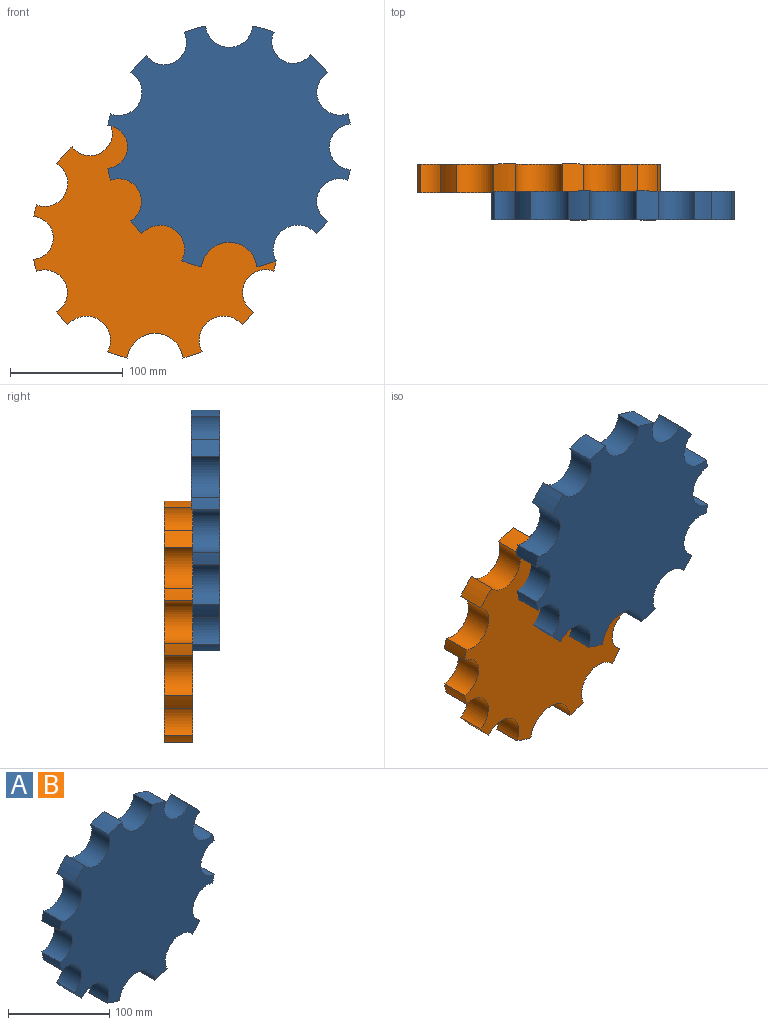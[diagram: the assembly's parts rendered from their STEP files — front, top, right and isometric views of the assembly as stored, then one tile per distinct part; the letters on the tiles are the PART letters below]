
ASSEMBLY  parts=2 mates=1
PART A: 26 faces, bbox 215.3x25.4x214 mm
  f0: cylinder r=19.08mm len=38.02mm, axis (0,1,0), area 1438.2mm2, adj f1,f23,f24,f25
  f1: cylinder r=109.44mm len=25.4mm, axis (0,1,0), area 278.4mm2, adj f0,f2,f24,f25
  f2: cylinder r=20.18mm len=37.37mm, axis (0,1,0), area 1515.7mm2, adj f1,f3,f24,f25
  f3: cylinder r=109.44mm len=25.4mm, axis (0,1,0), area 389mm2, adj f2,f4,f24,f25
  f4: cylinder r=21.37mm len=37.87mm, axis (0,1,0), area 1599.3mm2, adj f3,f5,f24,f25
  f5: cylinder r=109.44mm len=25.4mm, axis (0,1,0), area 469mm2, adj f4,f6,f24,f25
  f6: cylinder r=24.77mm len=49.23mm, axis (0,1,0), area 1834.1mm2, adj f5,f7,f24,f25
  f7: cylinder r=109.44mm len=25.4mm, axis (0,1,0), area 456mm2, adj f6,f8,f24,f25
  f8: cylinder r=21.61mm len=38.3mm, axis (0,1,0), area 1615.6mm2, adj f7,f9,f24,f25
  f9: cylinder r=109.44mm len=25.4mm, axis (0,1,0), area 385.3mm2, adj f8,f10,f24,f25
  f10: cylinder r=20.37mm len=37.7mm, axis (0,1,0), area 1528.7mm2, adj f9,f11,f24,f25
  f11: cylinder r=109.44mm len=25.4mm, axis (0,1,0), area 240.3mm2, adj f10,f12,f24,f25
  f12: cylinder r=20.39mm len=40.61mm, axis (0,1,0), area 1530.8mm2, adj f11,f13,f24,f25
  f13: cylinder r=109.44mm len=25.4mm, axis (0,1,0), area 242.9mm2, adj f12,f14,f24,f25
  f14: cylinder r=20.26mm len=37.51mm, axis (0,1,0), area 1521.4mm2, adj f13,f15,f24,f25
  f15: cylinder r=109.44mm len=25.4mm, axis (0,1,0), area 563mm2, adj f14,f16,f24,f25
  f16: cylinder r=19.18mm len=34.61mm, axis (0,1,0), area 1444.7mm2, adj f15,f17,f24,f25
  f17: cylinder r=109.44mm len=25.4mm, axis (0,1,0), area 500mm2, adj f16,f18,f24,f25
  f18: cylinder r=21.05mm len=41.9mm, axis (0,1,0), area 1576.6mm2, adj f17,f19,f24,f25
  f19: cylinder r=109.44mm len=25.4mm, axis (0,1,0), area 508mm2, adj f18,f20,f24,f25
  f20: cylinder r=19.88mm len=35.73mm, axis (0,1,0), area 1494.6mm2, adj f19,f21,f24,f25
  f21: cylinder r=109.44mm len=25.4mm, axis (0,1,0), area 511.4mm2, adj f20,f22,f24,f25
  f22: cylinder r=20.56mm len=38.05mm, axis (0,1,0), area 1542.4mm2, adj f21,f23,f24,f25
  f23: cylinder r=109.44mm len=25.4mm, axis (0,1,0), area 268.7mm2, adj f0,f22,f24,f25
  f24: plane 215.31x214.05mm, normal (0,-1,0), area 29822mm2, adj f0,f1,f2,f3,f4,f5,f6,f7
  f25: plane 215.31x214.05mm, normal (0,1,0), area 29822mm2, adj f0,f1,f2,f3,f4,f5,f6,f7
PART B: same geometry as A
PLACE A t=(13.67,6.14,-298.62)mm
PLACE B t=(-52.17,30.27,-379.5)mm
MATE slider B.f24 <-> A.f24  axis (0,-1,0) through (55.37,4.87,-399.81)mm
